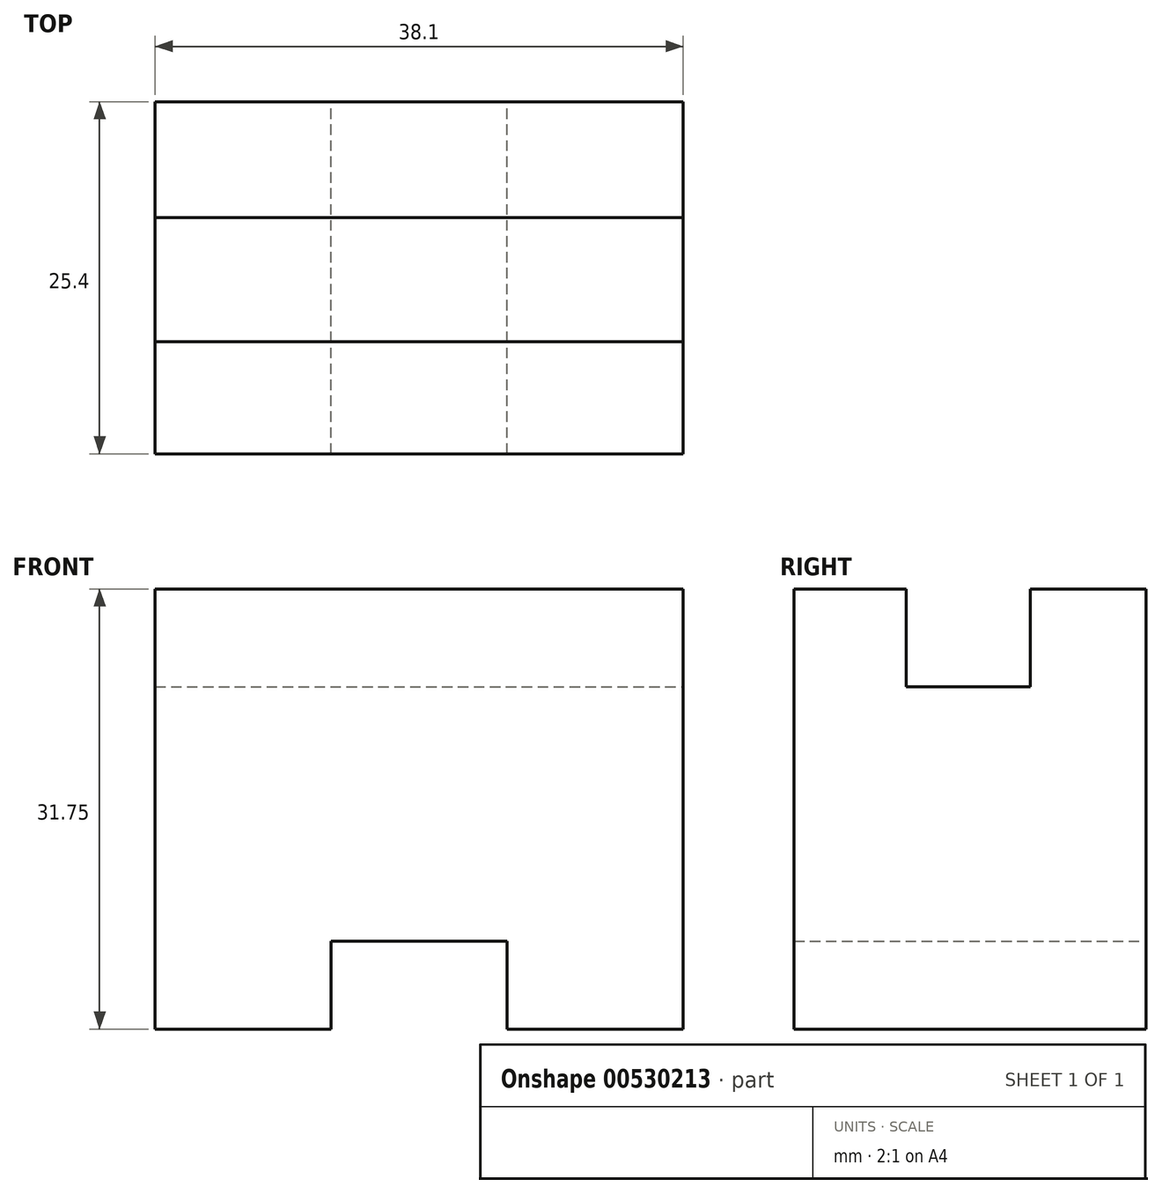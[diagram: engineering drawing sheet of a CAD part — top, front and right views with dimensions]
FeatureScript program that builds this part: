
annotation { "Feature Type Name" : "Feature", "Feature Type Description" : "" }
export const myFeature = defineFeature(function(context is Context, id is Id, definition is map)
    precondition{}
    {
        {
            var Q0;
            Q0=qCreatedBy(makeId("Front.planeOp"),FACE);
            var sketch = newSketch(context, id + "F0", { "sketchPlane" : qUnion([Q0])});
            skLineSegment(sketch, "E0", {"start": v(-65.36, 0) * mm, "end": v(-52.66, 0) * mm});
            skLineSegment(sketch, "E1", {"start": v(-52.66, 0) * mm, "end": v(-52.66, 6.35) * mm});
            skLineSegment(sketch, "E2", {"start": v(-52.66, 6.35) * mm, "end": v(-39.96, 6.35) * mm});
            skLineSegment(sketch, "E3", {"start": v(-39.96, 6.35) * mm, "end": v(-39.96, 0) * mm});
            skLineSegment(sketch, "E4", {"start": v(-39.96, 0) * mm, "end": v(-27.26, 0) * mm});
            skLineSegment(sketch, "E5", {"start": v(-27.26, 0) * mm, "end": v(-27.26, 31.75) * mm});
            skLineSegment(sketch, "E6", {"start": v(-27.26, 31.75) * mm, "end": v(-65.36, 31.75) * mm});
            skLineSegment(sketch, "E7", {"start": v(-65.36, 31.75) * mm, "end": v(-65.36, 0) * mm});
            skSolve(sketch);
        }
        {
            var Q0;
            Q0=makeQuery(id+"F0.imprint","IMPRINT",FACE,{"disambiguationData":[TD([[makeQuery(id+"F0.imprint","IMPRINT",EDGE,{"derivedFrom":sQuery(id+"F0.wireOp",EDGE,"E0")}),1.0]])]});
            extrude(context, id + "F1", {"entities" : qUnion([Q0]), "depth" : 25.4 * mm, "offsetDistance" : 25.4 * mm});
        }
        {
            var Q0;
            Q0=makeQuery(id+"F1.opExtrude","SWEPT_FACE",FACE,{"disambiguationData":[OSD([sQuery(id+"F0.wireOp",EDGE,"E5")])]});
            var sketch = newSketch(context, id + "F2", { "sketchPlane" : qUnion([Q0])});
            skLineSegment(sketch, "E8", {"start": v(-25.4, 31.75) * mm, "end": v(-17.31, 31.75) * mm});
            skLineSegment(sketch, "E9", {"start": v(-17.31, 31.75) * mm, "end": v(-17.31, 24.7) * mm});
            skLineSegment(sketch, "E10", {"start": v(-17.31, 24.7) * mm, "end": v(-8.35, 24.7) * mm});
            skLineSegment(sketch, "E11", {"start": v(-8.35, 24.7) * mm, "end": v(-8.35, 31.75) * mm});
            skLineSegment(sketch, "E12", {"start": v(-8.35, 31.75) * mm, "end": v(0, 31.75) * mm});
            skSolve(sketch);
        }
        {
            var Q0;
            {var subQ0=sQuery(id+"F2.wireOp",EDGE,"E9");Q0=makeQuery(id+"F2.imprint","IMPRINT",FACE,{"disambiguationData":[TD([[makeQuery(id+"F2.imprint","IMPRINT",EDGE,{"derivedFrom":subQ0}),1.0]])]});}
            extrude(context, id + "F3", {"entities" : qUnion([Q0]), "operationType" : NewBodyOperationType.REMOVE, "oppositeDirection" : true, "depth" : 76.2 * mm, "offsetDistance" : 25.4 * mm});
        }
    });
